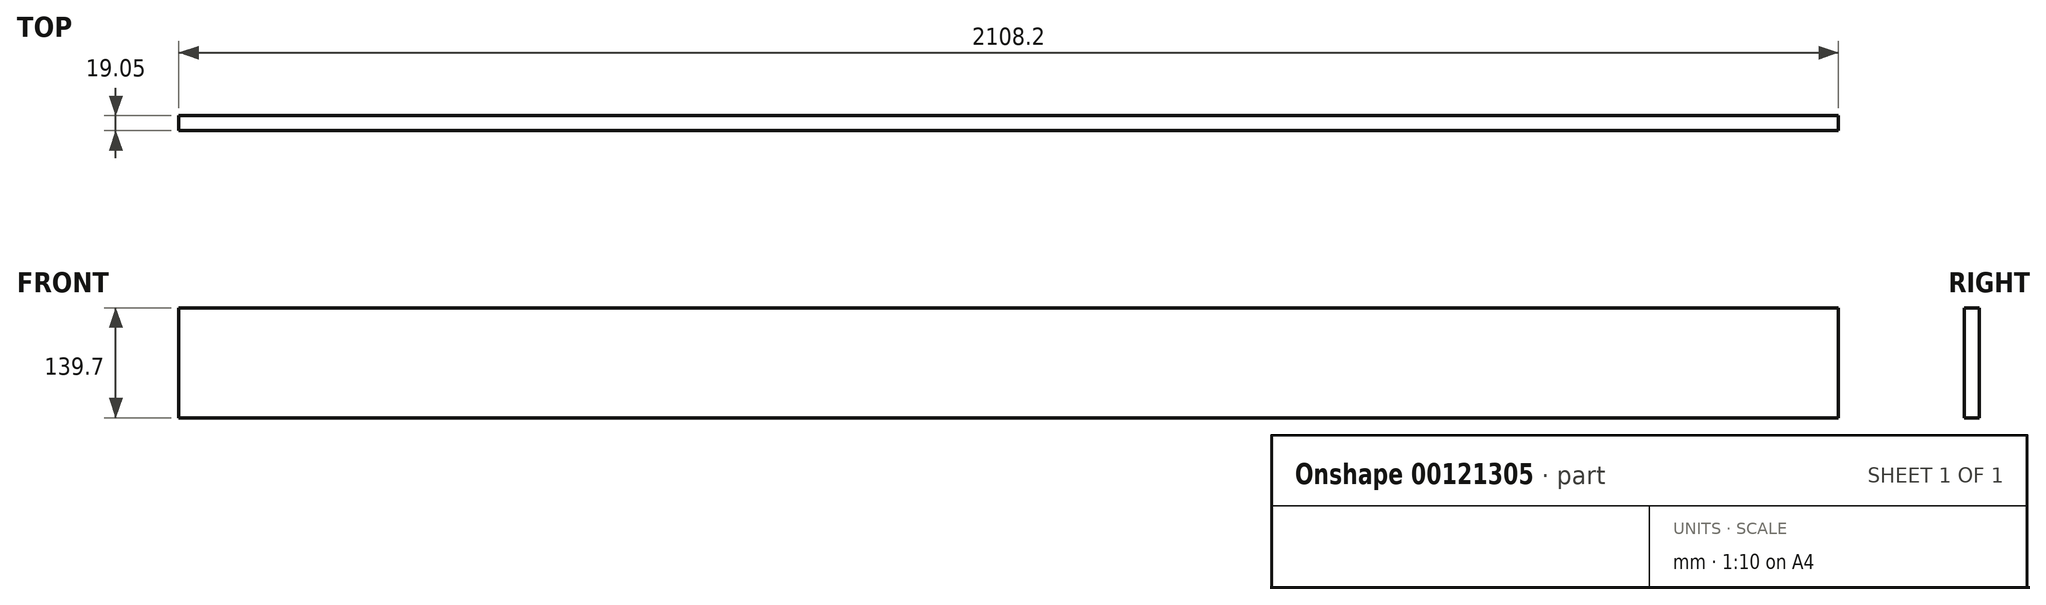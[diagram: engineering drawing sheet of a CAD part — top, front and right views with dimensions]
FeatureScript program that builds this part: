
annotation { "Feature Type Name" : "Feature", "Feature Type Description" : "" }
export const myFeature = defineFeature(function(context is Context, id is Id, definition is map)
    precondition{}
    {
        {
            var Q0;
            Q0=qCreatedBy(makeId("Front.planeOp"),FACE);
            var sketch = newSketch(context, id + "F0", { "sketchPlane" : qUnion([Q0])});
            skLineSegment(sketch, "E0.bottom", {"start": v(0, 0) * mm, "end": v(2108.2, 0) * mm});
            skLineSegment(sketch, "E0.top", {"start": v(0, 139.7) * mm, "end": v(2108.2, 139.7) * mm});
            skLineSegment(sketch, "E0.left", {"start": v(0, 0) * mm, "end": v(0, 139.7) * mm});
            skLineSegment(sketch, "E0.right", {"start": v(2108.2, 0) * mm, "end": v(2108.2, 139.7) * mm});
            skSolve(sketch);
        }
        {
            var Q0;
            Q0=makeQuery(id+"F0.imprint","IMPRINT",FACE,{"disambiguationData":[TD([[makeQuery(id+"F0.imprint","IMPRINT",EDGE,{"derivedFrom":sQuery(id+"F0.wireOp",EDGE,"E0.bottom")}),1.0]])]});
            extrude(context, id + "F1", {"entities" : qUnion([Q0]), "depth" : 19.05 * mm});
        }
    });
